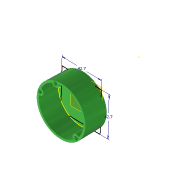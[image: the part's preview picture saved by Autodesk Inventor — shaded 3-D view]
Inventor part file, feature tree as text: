
AUTODESK INVENTOR PART (.ipt)
format: ipt  version: 2022 (Build 260153000, 153)  size: 356,352 bytes
history: native  units: in
note: dims shown in document units (in); Inventor stores cm internally (conversion verified against a paired STEP export)
features: plane x7, sketch x7, extrude x6, other x4, fillet x1, projected_geometry x1
ambient origin geometry x8: Origin, YZ Plane, XZ Plane, XY Plane, X Axis, Y Axis, Z Axis, Center Point
bodies: Solid1 (feature_tree)
feature tree (26):
  plane  "Arbeitsebene6"
  extrude  "Extrusion1"  Depth=0.0787in
  plane  "Arbeitsebene3"
  extrude  "Extrusion6"  Depth=0.1102in
  plane  "Arbeitsebene2"
  plane  "Arbeitsebene7"
  sketch  "Skizze16"  dims[d35=0.0in d36=0.0in d81=0.0591in]
  plane  "Arbeitsebene5"
  extrude  "Extrusion14"  Depth=0.0591in
  extrude  "Extrusion17"  Depth=0.0069in
  extrude  "Extrusion19"  Depth=0.1575in
  sketch  "Skizze26"  dims[d107=0.0001in d108=-0.0069in d111=0.1614in d112=0.1614in]
  other  "Arbeitsachse1"
  other  "Arbeitsachse2"
  other  "Arbeitspunkt1"
  other  "Arbeitspunkt2"
  plane  "Arbeitsebene8"
  plane  "Arbeitsebene9"
  extrude  "Extrusion24"  Depth=0.1614in
  fillet  "Rundung3"  Radius=0.1614in
  sketch  "Sketch1"  dims[d0=0.0787in d1=-0.0069in d2=0.315in]
  sketch  "Sketch8"  dims[d33=0.1102in d34=0.1102in]
  sketch  "Skizze19"  dims[d82=0.3937in d83=0.0069in d104=0.1575in]
  sketch  "Skizze21"  dims[d105=0.1575in d106=0.1575in]
  projected_geometry  "Projizierte Kontur6"
  sketch  "Skizze27"  dims[d113=0.1614in d114=0.1969in d115=-0.0069in d122=0.9055in d123=0.4528in d124=1.8701in d125=0.2756in d141=1.6811in d142=1.6811in d143=0.6299in d144=0.1969in d145=0.0in d146=0.0787in d78=0.0197in d79=0.0344in d80=0.0197in d95=0.0197in d96=0.0344in d97=0.0197in d98=0.0344in]
